# Revit family: Pro-Series-II-Drying-Tumbler_ContinentalGirbau
name_source: partatom
category: Mechanical Equipment
units: mm (PartAtom-declared; Revit-internal decimal feet)

## family parameters
Always vertical = Yes
Classification Number = 23.45.70.11.14.17
Cut with Voids When Loaded = No
Maintain Annotation Orientation = No
Part Type = Normal
Room Calculation Point = No
Round Connector Dimension = Use Radius
Shared = No
Work Plane-Based = No

## types (1)
- As Specified
    Assembly Code = E1010610
    Capacity_Volume = 8.3 CF
    Capacity_Weight = 30
    Construction Details = http://www.arcat.com
    CylRad = 1' - 1 1/4"
    Cyl_Depth = 2' - 2"
    Cyl_Diam = 2' - 2 1/2"
    DO2 = 0' - 11 11/32"
    Default Elevation = 0' - 0"
    Description = Commercial Washer
    DoorHeight = 2' - 3 1/2"
    DoorOpening = 1' - 10 11/16"
    Expected Lifespan (Years) = 0
    Fr_FaceWdth = 0' - 4 21/32"
    GlassCL = 0' - 9 11/32"
    Green Building-LEED = http://www.arcat.com
    InstWidth = 1' - 6"
    Installation Phase = Interior Fittings
    Keynote = 11 23 00
    LwrPanHt = 1' - 9 9/32"
    MachDepth = 3' - 4 7/8"
    MachHeight = 5' - 3 7/8"
    MachWidth = 2' - 4"
    Maintenance Schedule (Months) = 0
    Manufacturer = Continental Girbau, Inc.
    Manufacturer Fax = 920-231-4666
    Manufacturer Website = http://www.continentalgirbau.com
    Mech_Gas_Inlet = 0' - 0 1/2"
    Mech_Steam = 0' - 0"
    Mech_Waste = 0' - 8"
    Model = Generic
    OpeningCL = 0' - 11 11/32"
    Product Data = http://www.arcat.com
    Product Properties = http://www.arcat.com
    Send Message = http://admin.arcat.com &mf=
    Shell Material = Stainless Steel
    Single Phase = 0 VA
    SpecWizard = http://www.arcat.com
    Specification = http://www.arcat.com
    Three Phase = 0 VA
    Trim Material = Painted Metal - Black
    URL = http://www.continentalgirbau.com
    Voltage = 0 V
    Warranty Duration (Years) = 0

## geometry (parser evidence)
native form markers: Sweep x2
no freeform markers — native parametric forms only
